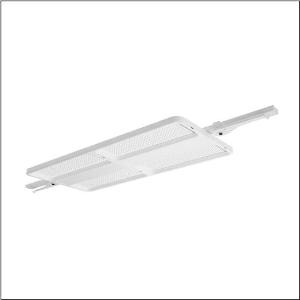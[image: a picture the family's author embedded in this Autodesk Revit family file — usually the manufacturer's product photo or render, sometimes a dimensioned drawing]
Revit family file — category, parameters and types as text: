
# Revit family: highbay_11_fur_modario_tragschiene_maxi_51hn12db3tma
name_source: partatom
category: Lighting Fixtures
units: mm (PartAtom-declared; Revit-internal decimal feet)

## family parameters
Cut with Voids When Loaded = No
Host = Face
Light Source = No
Part Type = Normal
Room Calculation Point = No
Round Connector Dimension = Use Diameter
Shared = No

## types (1)
- --- (1 x LED, 53070 lm, 295.1 W, 3000K)
    Apparent Load = 295 VA
    CIE Flux Codes = 87 98 100 100 100
    Color Rendering = 80
    Color Temperature = 3000K
    Default Elevation = 1800 mm
    Description = high bay luminaire Highbay 11 for Modario trunking rail maxi; direct symmetric wide distribution, light control with lens of PMMA; UGR ≤ 22 (X = 4H | Y = 8H | S = 0.25H | reflection values 70/50/20); luminous flux: 53.070lm; light colour: 830, colour temperature: 3000K, MacAdam ≤ 2 SDCM (initial), colour rendering: CRI > 80; luminous efficacy: 179,8lm/W; rated service life: 100.000h (L95) at AT= 25°C; control: DALI 2; luminaire connection: plug, 5-pole, with phase selectionmains connection: 230..240V, AC 50/60Hz; connected load: 295,1W; protection rating (complete): IP64; insulation class (complete): insulation class I (protective earthing); protection symbol: D; impact resistance: IK06; certification: CE, UKCA; internal wiring halogen-free; luminaire LABS conformity tested according to VDMA 24364:2018-05; Suitable for use in the food industry according to the specifications of IFS-Food, HACCP and/or BRC; housing frame of high-performance plastic PA6, matt traffic white (RAL 9016); cover of PMMA; fixing on rail side of steel, galvanised, white; blank cover of PC, traffic white (RAL 9016); dimension (LxWxH): 1.496 x 442 x 72mm; permissible operating ambient temperature: -40..+50°C (reducing of maximum allowable ambient temperature of 5°C with ceiling mounting); packaging unit: 1 piece
    Height = 72 mm  [stored 0.23622 ft]
    Lamp = 1 x LED
    Lamp Light Flux = 53070 lm
    Lamp Power = 295.1 W
    Lamp count = 1
    Length = 946 mm
    Luminous efficacy = 180 lm/W
    Manufacturer = Siteco
    ModVariant = No
    Model = 51HN12DB3TMA
    Mounting Place = Ceiling
    Mounting Type = Pendant
    Number of Poles = 1
    OnlyDefault = Yes
    Power Factor = 1
    Product Name = Highbay 11 für Modario Tragschiene maxi
    Product group = high bay luminaire
    ProductGroupID = 902
    Protection Class = Protection class I
    Protection Degree = IP 64
    RLX_Detail_Level = 1
    RLX_Emergency_Light_Flux = 0 lm
    RLX_Emergency_Type = 0
    RLX_Emergency_Type_DB = No
    RlxData = <blob elided: 21321 chars, md5=d1d18840>
    Socket = socket
    Standby Power = 0 W
    System Light Flux = 53071 lm
    System Power = 295 W
    Type Comments = factory setting: luminous flux: 100 % | dim-lin: 254 | 664 mA
    Type Image = l_1363248.jpg
    URL = http://relux.com
    VarID = @adj_008693
    Voltage = 0 V
    Weight = 0.00 kg
    Width = 442 mm

note: [stored X ft] marks values corroborated as IEEE doubles in the binary element streams (Revit-internal decimal feet)

## geometry (parser evidence)
native form markers: Blend x4, Sweep x13
no freeform markers — native parametric forms only
